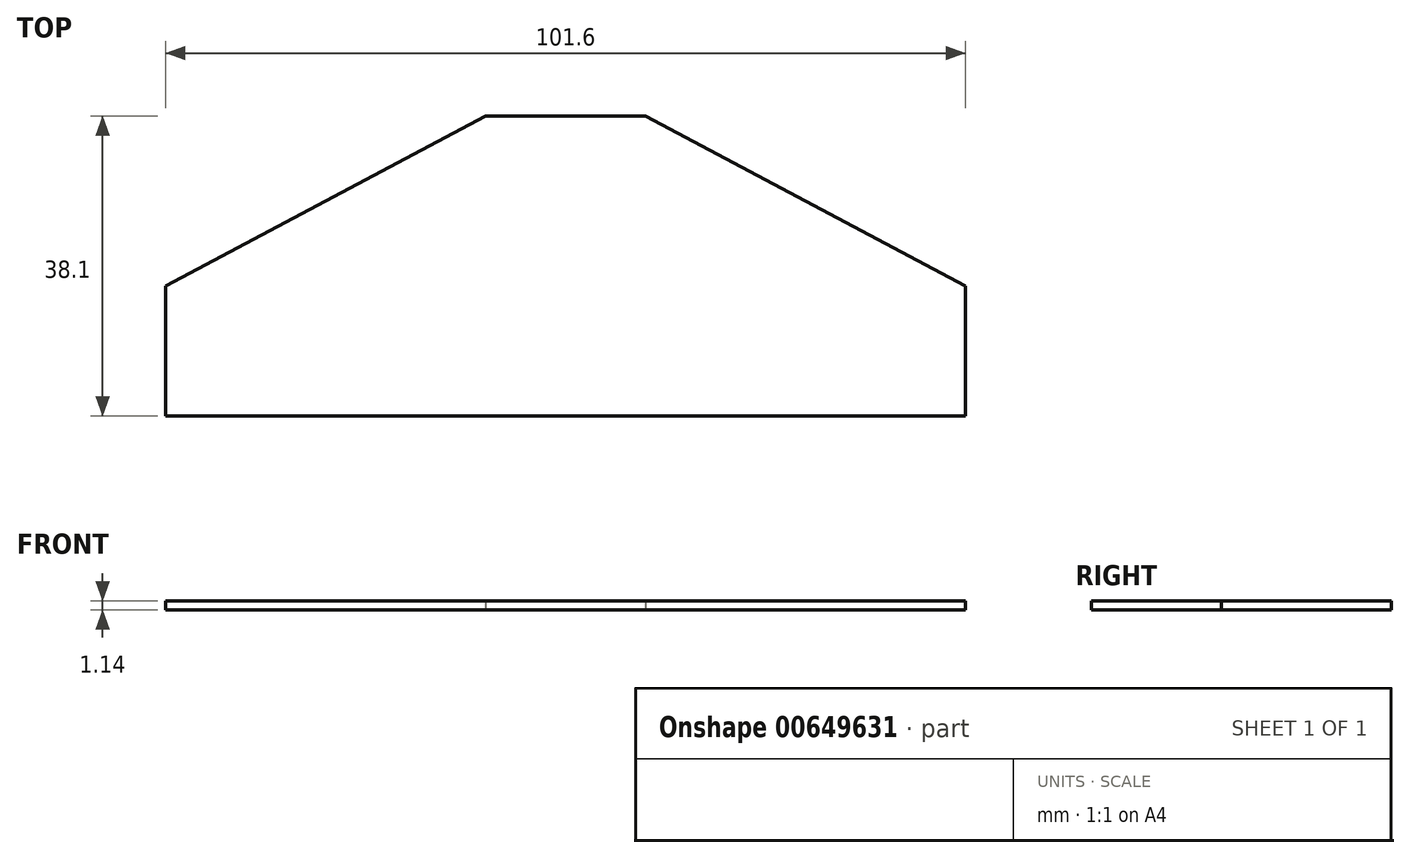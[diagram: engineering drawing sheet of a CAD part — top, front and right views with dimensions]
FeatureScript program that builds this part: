
annotation { "Feature Type Name" : "Feature", "Feature Type Description" : "" }
export const myFeature = defineFeature(function(context is Context, id is Id, definition is map)
    precondition{}
    {
        {
            var Q0;
            Q0=qCreatedBy(makeId("Top.planeOp"),FACE);
            var sketch = newSketch(context, id + "F0", { "sketchPlane" : qUnion([Q0])});
            skLineSegment(sketch, "E0", {"start": v(0, 0) * mm, "end": v(0, 38.1) * mm, "construction": true});
            skLineSegment(sketch, "E1", {"start": v(0, 38.1) * mm, "end": v(-10.16, 38.1) * mm});
            skLineSegment(sketch, "E2", {"start": v(-10.16, 38.1) * mm, "end": v(-50.8, 16.51) * mm});
            skLineSegment(sketch, "E3", {"start": v(-50.8, 16.51) * mm, "end": v(-50.8, 0) * mm});
            skLineSegment(sketch, "E4", {"start": v(-50.8, 0) * mm, "end": v(0, 0) * mm});
            skLineSegment(sketch, "E5.MirrorCS", {"start": v(0, 38.1) * mm, "end": v(10.16, 38.1) * mm});
            skLineSegment(sketch, "E6.MirrorCS", {"start": v(10.16, 38.1) * mm, "end": v(50.8, 16.51) * mm});
            skLineSegment(sketch, "E7.MirrorCS", {"start": v(50.8, 16.51) * mm, "end": v(50.8, 0) * mm});
            skLineSegment(sketch, "E8.MirrorCS", {"start": v(50.8, 0) * mm, "end": v(0, 0) * mm});
            skSolve(sketch);
        }
        {
            var Q0;
            Q0=makeQuery(id+"F0.imprint","IMPRINT",FACE,{"disambiguationData":[TD([[makeQuery(id+"F0.imprint","IMPRINT",EDGE,{"derivedFrom":sQuery(id+"F0.wireOp",EDGE,"E1")}),1.0]])]});
            extrude(context, id + "F1", {"entities" : qUnion([Q0]), "depth" : 1.14 * mm, "offsetDistance" : 25.4 * mm});
        }
    });
